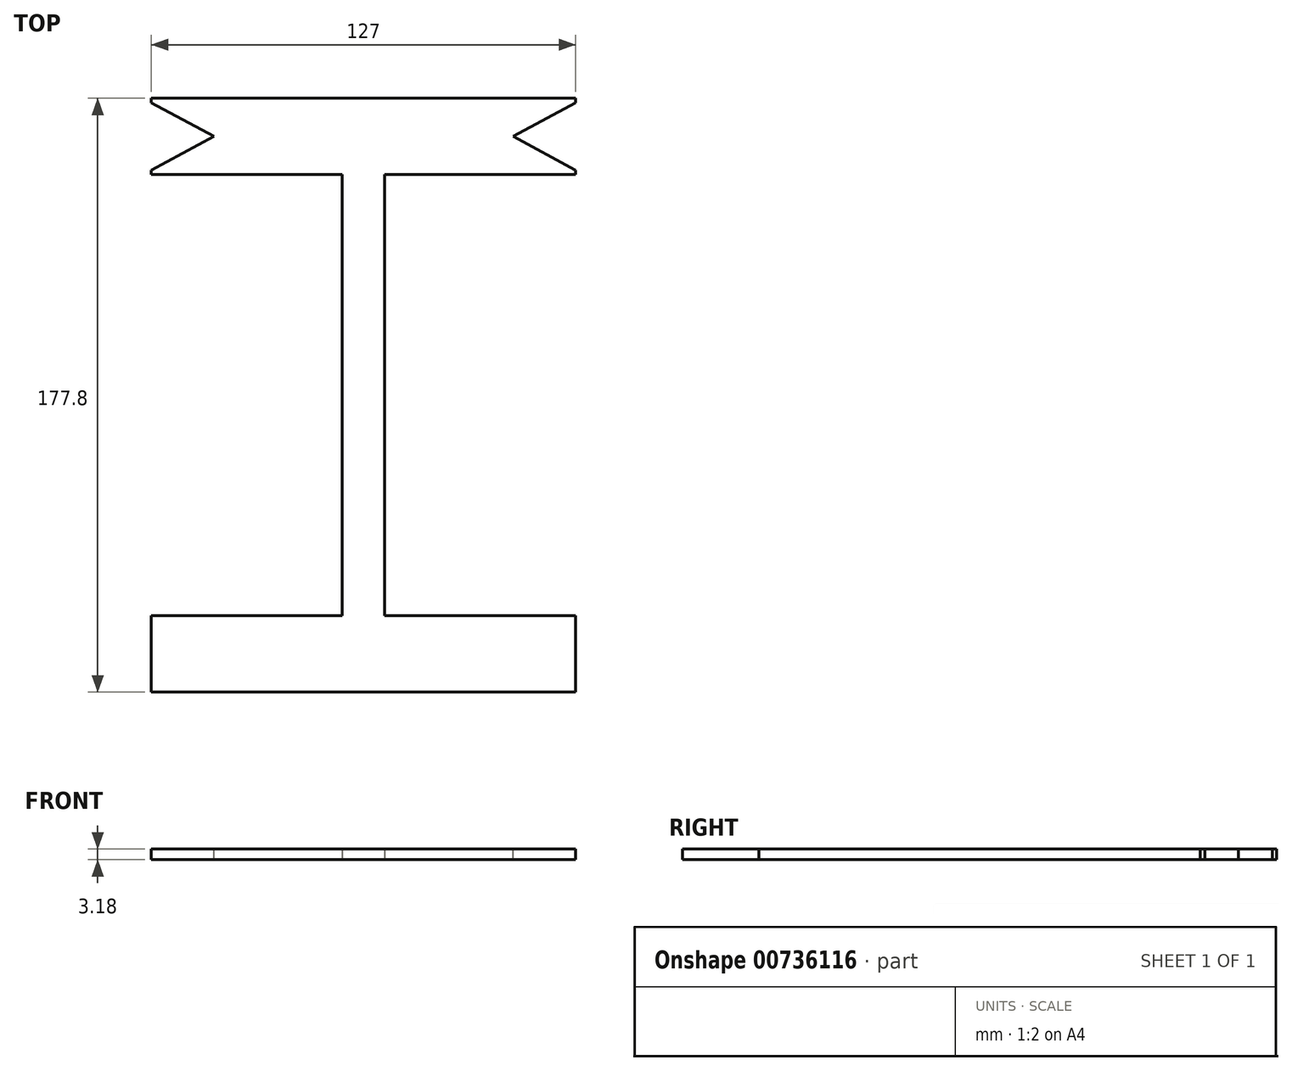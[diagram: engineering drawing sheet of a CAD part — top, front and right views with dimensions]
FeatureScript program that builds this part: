
annotation { "Feature Type Name" : "Feature", "Feature Type Description" : "" }
export const myFeature = defineFeature(function(context is Context, id is Id, definition is map)
    precondition{}
    {
        {
            var Q0;
            Q0=qCreatedBy(makeId("Top.planeOp"),FACE);
            var sketch = newSketch(context, id + "F0", { "sketchPlane" : qUnion([Q0])});
            skLineSegment(sketch, "E0.bottom", {"start": v(-98.45, 56.9) * mm, "end": v(28.55, 56.9) * mm});
            skLineSegment(sketch, "E0.top", {"start": v(-98.45, -120.9) * mm, "end": v(28.55, -120.9) * mm});
            skLineSegment(sketch, "E0.left", {"start": v(-98.45, 56.9) * mm, "end": v(-98.45, -120.9) * mm});
            skLineSegment(sketch, "E0.right", {"start": v(28.55, 56.9) * mm, "end": v(28.55, -120.9) * mm});
            skPoint(sketch, "E1", {"position": v(-98.45, 34.05) * mm});
            skPoint(sketch, "E2", {"position": v(-98.45, -98.03) * mm});
            skLineSegment(sketch, "E3", {"start": v(-98.45, -98.03) * mm, "end": v(28.55, -98.03) * mm});
            skLineSegment(sketch, "E4", {"start": v(-98.45, 34.05) * mm, "end": v(28.55, 34.05) * mm});
            skPoint(sketch, "E5", {"position": v(-34.95, 34.05) * mm});
            skPoint(sketch, "E6", {"position": v(-38.12, 34.05) * mm});
            skPoint(sketch, "E7", {"position": v(-41.3, 34.05) * mm});
            skPoint(sketch, "E8", {"position": v(-98.45, -32) * mm});
            skLineSegment(sketch, "E9", {"start": v(-98.45, -32) * mm, "end": v(28.55, -32) * mm, "construction": true});
            skPoint(sketch, "E10.MirrorP", {"position": v(-38.12, -98.03) * mm});
            skPoint(sketch, "E11.MirrorP", {"position": v(-41.3, -98.03) * mm});
            skPoint(sketch, "E12.MirrorP", {"position": v(-31.77, 34.05) * mm});
            skPoint(sketch, "E13.MirrorP", {"position": v(-28.6, 34.05) * mm});
            skLineSegment(sketch, "E14", {"start": v(-41.3, -98.03) * mm, "end": v(-41.3, 34.05) * mm});
            skLineSegment(sketch, "E15.MirrorCS", {"start": v(-28.6, -98.03) * mm, "end": v(-28.6, 34.05) * mm});
            skLineSegment(sketch, "E16.bottom", {"start": v(-46.38, -28.48) * mm, "end": v(-43.2, -28.48) * mm});
            skLineSegment(sketch, "E16.top", {"start": v(-46.38, -38.48) * mm, "end": v(-43.2, -38.48) * mm});
            skLineSegment(sketch, "E16.left", {"start": v(-46.38, -28.48) * mm, "end": v(-46.38, -38.48) * mm});
            skLineSegment(sketch, "E16.right", {"start": v(-43.2, -28.48) * mm, "end": v(-43.2, -38.48) * mm});
            skPoint(sketch, "E17", {"position": v(-43.2, -33.48) * mm});
            skLineSegment(sketch, "E18.MirrorCS", {"start": v(-23.52, -28.48) * mm, "end": v(-26.7, -28.48) * mm});
            skLineSegment(sketch, "E19.MirrorCS", {"start": v(-26.7, -28.48) * mm, "end": v(-26.7, -38.48) * mm});
            skLineSegment(sketch, "E20.MirrorCS", {"start": v(-23.52, -28.48) * mm, "end": v(-23.52, -38.48) * mm});
            skLineSegment(sketch, "E21.MirrorCS", {"start": v(-23.52, -38.48) * mm, "end": v(-26.7, -38.48) * mm});
            skSolve(sketch);
        }
        {
            var Q0;
            {var subQ4=sQuery(id+"F0.wireOp",EDGE,"E0.bottom");Q0=makeQuery(id+"F0.imprint","IMPRINT",FACE,{"disambiguationData":[TD([[makeQuery(id+"F0.imprint","IMPRINT",EDGE,{"derivedFrom":subQ4}),-1.0]])]});}
            var Q1;
            {var subQ5=sQuery(id+"F0.wireOp",EDGE,"W9d6LSSu-lLYZ-PWI0-D8CJ-yOae8zQJ0DPb");Q1=makeQuery(id+"F0.imprint","IMPRINT",FACE,{"disambiguationData":[TD([[makeQuery(id+"F0.imprint","IMPRINT",EDGE,{"derivedFrom":subQ5}),-1.0]])]});}
            var Q2;
            {var subQ5=sQuery(id+"F0.wireOp",EDGE,"e03ca8af-7ad5-417d-b2bf-2dffb811fbdc0.MirrorCS");Q2=makeQuery(id+"F0.imprint","IMPRINT",FACE,{"disambiguationData":[TD([[makeQuery(id+"F0.imprint","IMPRINT",EDGE,{"derivedFrom":subQ5}),1.0]])]});}
            var Q3;
            {var subQ0=sQuery(id+"F0.wireOp",EDGE,"E14");Q3=makeQuery(id+"F0.imprint","IMPRINT",FACE,{"disambiguationData":[TD([[makeQuery(id+"F0.imprint","IMPRINT",EDGE,{"derivedFrom":subQ0}),-1.0]])]});}
            var Q4;
            {var subQ5=sQuery(id+"F0.wireOp",EDGE,"E0.top");Q4=makeQuery(id+"F0.imprint","IMPRINT",FACE,{"disambiguationData":[TD([[makeQuery(id+"F0.imprint","IMPRINT",EDGE,{"derivedFrom":subQ5}),1.0]])]});}
            extrude(context, id + "F1", {"entities" : qUnion([Q0, Q1, Q2, Q3, Q4]), "depth" : 3.17 * mm, "offsetDistance" : 25.4 * mm});
        }
        {
            var Q0;
            Q0=makeQuery(id+"F1.opExtrude","CAP_FACE",FACE,{"disambiguationData":[OSD([sQuery(id+"F0.wireOp",EDGE,"E0.bottom"),sQuery(id+"F0.wireOp",EDGE,"E0.top"),sQuery(id+"F0.wireOp",EDGE,"E0.left"),sQuery(id+"F0.wireOp",EDGE,"E0.right"),sQuery(id+"F0.wireOp",EDGE,"E3"),sQuery(id+"F0.wireOp",EDGE,"E4"),sQuery(id+"F0.wireOp",EDGE,"W9d6LSSu-lLYZ-PWI0-D8CJ-yOae8zQJ0DPb"),sQuery(id+"F0.wireOp",EDGE,"E14"),sQuery(id+"F0.wireOp",EDGE,"E15.MirrorCS"),sQuery(id+"F0.wireOp",EDGE,"e03ca8af-7ad5-417d-b2bf-2dffb811fbdc0.MirrorCS")])],"isStart":false});
            var sketch = newSketch(context, id + "F2", { "sketchPlane" : qUnion([Q0])});
            skLineSegment(sketch, "E22", {"start": v(-11.43, 56.9) * mm, "end": v(28.55, 35.38) * mm});
            skLineSegment(sketch, "E23", {"start": v(-98.45, 35.38) * mm, "end": v(-58.46, 56.9) * mm});
            skLineSegment(sketch, "E24", {"start": v(-98.45, 35.38) * mm, "end": v(28.55, 35.38) * mm, "construction": true});
            skLineSegment(sketch, "E25", {"start": v(-11.43, 56.9) * mm, "end": v(28.55, 56.9) * mm});
            skLineSegment(sketch, "E26", {"start": v(28.55, 56.9) * mm, "end": v(28.55, 35.38) * mm});
            skLineSegment(sketch, "E27", {"start": v(-98.45, 35.38) * mm, "end": v(-98.45, 56.9) * mm});
            skLineSegment(sketch, "E28", {"start": v(-98.45, 56.9) * mm, "end": v(-58.46, 56.9) * mm});
            skLineSegment(sketch, "E29", {"start": v(-98.45, 45.48) * mm, "end": v(28.55, 45.48) * mm});
            skLineSegment(sketch, "E30.MirrorCS", {"start": v(-98.45, 55.58) * mm, "end": v(-58.46, 34.05) * mm});
            skLineSegment(sketch, "E31.MirrorCS", {"start": v(-98.45, 34.05) * mm, "end": v(-58.46, 34.05) * mm});
            skLineSegment(sketch, "E32.MirrorCS", {"start": v(-98.45, 55.58) * mm, "end": v(-98.45, 34.05) * mm});
            skLineSegment(sketch, "E33.MirrorCS", {"start": v(-11.43, 34.05) * mm, "end": v(28.55, 55.58) * mm});
            skLineSegment(sketch, "E34.MirrorCS", {"start": v(-11.43, 34.05) * mm, "end": v(28.55, 34.05) * mm});
            skLineSegment(sketch, "E35.MirrorCS", {"start": v(28.55, 34.05) * mm, "end": v(28.55, 55.58) * mm});
            skSolve(sketch);
        }
        {
            var Q0;
            Q0=makeQuery(id+"F2.imprint","IMPRINT",FACE,{"disambiguationData":[TD([[makeQuery(id+"F2.imprint","IMPRINT",EDGE,{"derivedFrom":sQuery(id+"F2.wireOp",EDGE,"E22")}),1.0]])]});
            var Q1;
            Q1=makeQuery(id+"F2.imprint","IMPRINT",FACE,{"disambiguationData":[TD([[makeQuery(id+"F2.imprint","IMPRINT",EDGE,{"derivedFrom":sQuery(id+"F2.wireOp",EDGE,"E23")}),1.0]])]});
            extrude(context, id + "F3", {"entities" : qUnion([Q0, Q1]), "operationType" : NewBodyOperationType.REMOVE, "oppositeDirection" : true, "depth" : 25.4 * mm, "offsetDistance" : 25.4 * mm});
        }
        {
            var Q0;
            Q0=makeQuery(id+"F2.imprint","IMPRINT",FACE,{"disambiguationData":[TD([[makeQuery(id+"F2.imprint","IMPRINT",EDGE,{"derivedFrom":sQuery(id+"F2.wireOp",EDGE,"E30.MirrorCS")}),-1.0]])]});
            var Q1;
            Q1=makeQuery(id+"F2.imprint","IMPRINT",FACE,{"disambiguationData":[TD([[makeQuery(id+"F2.imprint","IMPRINT",EDGE,{"derivedFrom":sQuery(id+"F2.wireOp",EDGE,"E33.MirrorCS")}),-1.0]])]});
            extrude(context, id + "F4", {"entities" : qUnion([Q0, Q1]), "operationType" : NewBodyOperationType.REMOVE, "oppositeDirection" : true, "depth" : 25.4 * mm, "offsetDistance" : 25.4 * mm});
        }
    });
